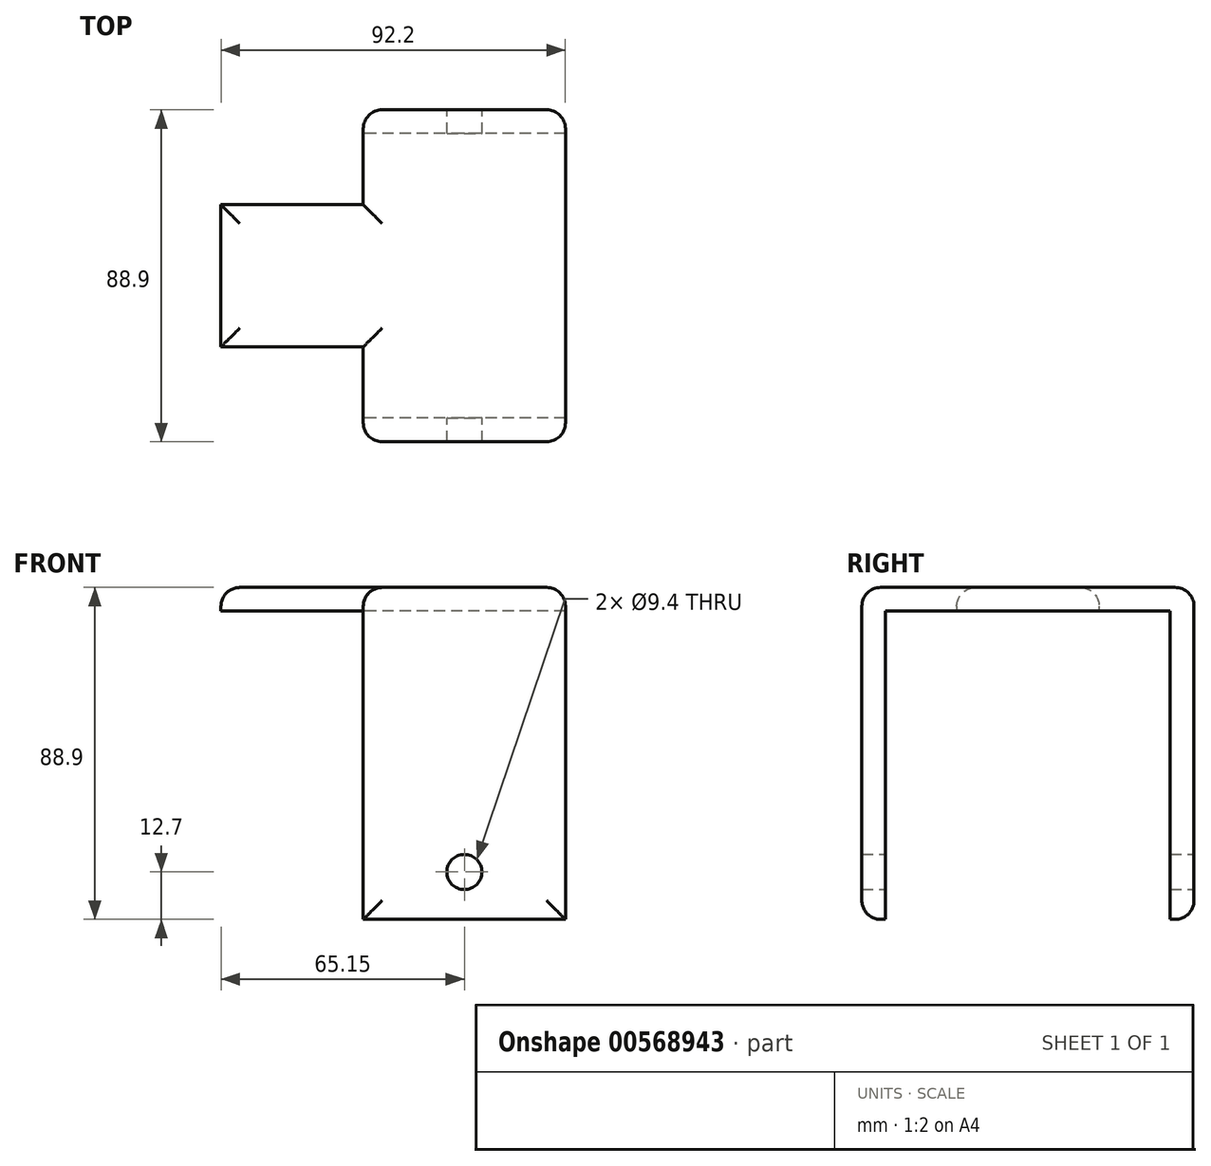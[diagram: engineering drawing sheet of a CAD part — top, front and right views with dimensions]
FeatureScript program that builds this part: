
annotation { "Feature Type Name" : "Feature", "Feature Type Description" : "" }
export const myFeature = defineFeature(function(context is Context, id is Id, definition is map)
    precondition{}
    {
        {
            var Q0;
            Q0=qCreatedBy(makeId("Front.planeOp"),FACE);
            var sketch = newSketch(context, id + "F0", { "sketchPlane" : qUnion([Q0])});
            skLineSegment(sketch, "E0.bottom", {"start": v(27.05, 44.45) * mm, "end": v(-27.05, 44.45) * mm});
            skLineSegment(sketch, "E0.top", {"start": v(27.05, -44.45) * mm, "end": v(-27.05, -44.45) * mm});
            skLineSegment(sketch, "E0.left", {"start": v(27.05, 44.45) * mm, "end": v(27.05, -44.45) * mm});
            skLineSegment(sketch, "E0.right", {"start": v(-27.05, 44.45) * mm, "end": v(-27.05, -44.45) * mm});
            skPoint(sketch, "E0.middle", {"position": v(0, 0) * mm});
            skSolve(sketch);
        }
        {
            var Q0;
            Q0=makeQuery(id+"F0.imprint","IMPRINT",FACE,{"disambiguationData":[TD([[makeQuery(id+"F0.imprint","IMPRINT",EDGE,{"derivedFrom":sQuery(id+"F0.wireOp",EDGE,"E0.bottom")}),1.0]])]});
            extrude(context, id + "F1", {"entities" : qUnion([Q0]), "depth" : 6.35 * mm, "offsetDistance" : 25.4 * mm});
        }
        {
            var Q0;
            Q0=makeQuery(id+"F1.opExtrude","CAP_FACE",FACE,{"disambiguationData":[OSD([sQuery(id+"F0.wireOp",EDGE,"E0.bottom"),sQuery(id+"F0.wireOp",EDGE,"E0.top"),sQuery(id+"F0.wireOp",EDGE,"E0.left"),sQuery(id+"F0.wireOp",EDGE,"E0.right")])],"isStart":true});
            var sketch = newSketch(context, id + "F2", { "sketchPlane" : qUnion([Q0])});
            skLineSegment(sketch, "E1.bottom", {"start": v(-27.05, 44.45) * mm, "end": v(27.05, 44.45) * mm});
            skLineSegment(sketch, "E1.top", {"start": v(-27.05, 38.1) * mm, "end": v(27.05, 38.1) * mm});
            skLineSegment(sketch, "E1.left", {"start": v(-27.05, 44.45) * mm, "end": v(-27.05, 38.1) * mm});
            skLineSegment(sketch, "E1.right", {"start": v(27.05, 44.45) * mm, "end": v(27.05, 38.1) * mm});
            skSolve(sketch);
        }
        {
            var Q0;
            Q0=makeQuery(id+"F2.imprint","IMPRINT",FACE,{"disambiguationData":[TD([[makeQuery(id+"F2.imprint","IMPRINT",EDGE,{"derivedFrom":sQuery(id+"F2.wireOp",EDGE,"E1.bottom")}),-1.0]])]});
            extrude(context, id + "F3", {"entities" : qUnion([Q0]), "operationType" : NewBodyOperationType.ADD, "depth" : 76.2 * mm, "offsetDistance" : 25.4 * mm});
        }
        {
            var Q0;
            Q0=makeQuery(id+"F3.opExtrude","CAP_FACE",FACE,{"disambiguationData":[OSD([sQuery(id+"F2.wireOp",EDGE,"E1.bottom"),sQuery(id+"F2.wireOp",EDGE,"E1.top"),sQuery(id+"F2.wireOp",EDGE,"E1.left"),sQuery(id+"F2.wireOp",EDGE,"E1.right")])],"isStart":false});
            var sketch = newSketch(context, id + "F4", { "sketchPlane" : qUnion([Q0])});
            skLineSegment(sketch, "E2.bottom", {"start": v(27.05, 44.45) * mm, "end": v(-27.05, 44.45) * mm});
            skLineSegment(sketch, "E2.top", {"start": v(27.05, -44.45) * mm, "end": v(-27.05, -44.45) * mm});
            skLineSegment(sketch, "E2.left", {"start": v(27.05, 44.45) * mm, "end": v(27.05, -44.45) * mm});
            skLineSegment(sketch, "E2.right", {"start": v(-27.05, 44.45) * mm, "end": v(-27.05, -44.45) * mm});
            skPoint(sketch, "E2.middle", {"position": v(0, 0) * mm});
            skSolve(sketch);
        }
        {
            var Q0;
            Q0 = qSketchRegion(id + "F4", true);
            extrude(context, id + "F5", {"entities" : qUnion([Q0]), "operationType" : NewBodyOperationType.ADD, "depth" : 6.35 * mm, "offsetDistance" : 25.4 * mm});
        }
        {
            var Q0;
            Q0=makeQuery(id+"F5.opExtrude","CAP_FACE",FACE,{"disambiguationData":[OSD([sQuery(id+"F4.wireOp",EDGE,"E2.bottom"),sQuery(id+"F4.wireOp",EDGE,"E2.top"),sQuery(id+"F4.wireOp",EDGE,"E2.left"),sQuery(id+"F4.wireOp",EDGE,"E2.right")])],"isStart":false});
            var sketch = newSketch(context, id + "F6", { "sketchPlane" : qUnion([Q0])});
            skLineSegment(sketch, "E3", {"start": v(0, -44.45) * mm, "end": v(0, -31.75) * mm, "construction": true});
            skCircle(sketch, "E4", {"center": v(0, -31.75) * mm, "radius": 4.7 * mm});
            skSolve(sketch);
        }
        {
            var Q0;
            Q0 = qSketchRegion(id + "F6", true);
            extrude(context, id + "F7", {"entities" : qUnion([Q0]), "operationType" : NewBodyOperationType.REMOVE, "oppositeDirection" : true, "depth" : 109.22 * mm, "offsetDistance" : 25.4 * mm});
        }
        {
            var Q0;
            Q0=makeQuery(id+"F5.boolean.opBoolean","MERGE",FACE,{"derivedFrom":[makeQuery(id+"F3.boolean.opBoolean","MERGE",FACE,{"derivedFrom":[makeQuery(id+"F1.opExtrude","SWEPT_FACE",FACE,{"disambiguationData":[OSD([sQuery(id+"F0.wireOp",EDGE,"E0.right")])]}),makeQuery(id+"F3.opExtrude","SWEPT_FACE",FACE,{"disambiguationData":[OSD([sQuery(id+"F2.wireOp",EDGE,"E1.right")])]})]}),makeQuery(id+"F5.opExtrude","SWEPT_FACE",FACE,{"disambiguationData":[OSD([sQuery(id+"F4.wireOp",EDGE,"E2.left")])]})]});
            var sketch = newSketch(context, id + "F8", { "sketchPlane" : qUnion([Q0])});
            skLineSegment(sketch, "E5", {"start": v(-38.1, 44.45) * mm, "end": v(-38.1, 38.1) * mm, "construction": true});
            skLineSegment(sketch, "E6.bottom", {"start": v(-19.05, 44.45) * mm, "end": v(-57.15, 44.45) * mm});
            skLineSegment(sketch, "E6.top", {"start": v(-19.05, 38.1) * mm, "end": v(-57.15, 38.1) * mm});
            skLineSegment(sketch, "E6.left", {"start": v(-19.05, 44.45) * mm, "end": v(-19.05, 38.1) * mm});
            skLineSegment(sketch, "E6.right", {"start": v(-57.15, 44.45) * mm, "end": v(-57.15, 38.1) * mm});
            skPoint(sketch, "E6.middle", {"position": v(-38.1, 41.28) * mm});
            skSolve(sketch);
        }
        {
            var Q0;
            Q0 = qSketchRegion(id + "F8", true);
            extrude(context, id + "F9", {"entities" : qUnion([Q0]), "operationType" : NewBodyOperationType.ADD, "depth" : 38.1 * mm, "offsetDistance" : 25.4 * mm});
        }
        {
            var Q0;
            Q0=makeQuery(id+"F5.opExtrude","CAP_EDGE",EDGE,{"disambiguationData":[OSD([sQuery(id+"F4.wireOp",EDGE,"E2.right")])],"isStart":false});
            var Q1;
            Q1=makeQuery(id+"F5.boolean.opBoolean","MERGE",EDGE,{"derivedFrom":[makeQuery(id+"F3.boolean.opBoolean","MERGE",EDGE,{"derivedFrom":[makeQuery(id+"F1.opExtrude","SWEPT_EDGE",EDGE,{"disambiguationData":[OSD([sQuery(id+"F0.wireOp",EDGE,"E0.bottom"),sQuery(id+"F0.wireOp",EDGE,"E0.left")])]}),makeQuery(id+"F3.opExtrude","SWEPT_EDGE",EDGE,{"disambiguationData":[OSD([sQuery(id+"F2.wireOp",EDGE,"E1.bottom"),sQuery(id+"F2.wireOp",EDGE,"E1.left")])]})]}),makeQuery(id+"F5.opExtrude","SWEPT_EDGE",EDGE,{"disambiguationData":[OSD([sQuery(id+"F4.wireOp",EDGE,"E2.bottom"),sQuery(id+"F4.wireOp",EDGE,"E2.right")])]})]});
            var Q2;
            Q2=makeQuery(id+"F5.opExtrude","CAP_EDGE",EDGE,{"disambiguationData":[OSD([sQuery(id+"F4.wireOp",EDGE,"E2.left")])],"isStart":false});
            var Q3;
            Q3=makeQuery(id+"F1.opExtrude","CAP_EDGE",EDGE,{"disambiguationData":[OSD([sQuery(id+"F0.wireOp",EDGE,"E0.right")])],"isStart":false});
            var Q4;
            Q4=makeQuery(id+"F1.opExtrude","CAP_EDGE",EDGE,{"disambiguationData":[OSD([sQuery(id+"F0.wireOp",EDGE,"E0.left")])],"isStart":false});
            var Q5;
            Q5=makeQuery(id+"F1.opExtrude","CAP_EDGE",EDGE,{"disambiguationData":[OSD([sQuery(id+"F0.wireOp",EDGE,"E0.top")])],"isStart":false});
            var Q6;
            Q6=makeQuery(id+"F5.opExtrude","CAP_EDGE",EDGE,{"disambiguationData":[OSD([sQuery(id+"F4.wireOp",EDGE,"E2.top")])],"isStart":false});
            var Q7;
            Q7=makeQuery(id+"F1.opExtrude","CAP_EDGE",EDGE,{"disambiguationData":[OSD([sQuery(id+"F0.wireOp",EDGE,"E0.bottom")])],"isStart":false});
            var Q8;
            Q8=makeQuery(id+"F5.opExtrude","CAP_EDGE",EDGE,{"disambiguationData":[OSD([sQuery(id+"F4.wireOp",EDGE,"E2.bottom")])],"isStart":false});
            var Q9;
            {var subQ0=sQuery(id+"F2.wireOp",EDGE,"E1.right");var subQ1=sQuery(id+"F4.wireOp",EDGE,"E2.bottom");var subQ2=sQuery(id+"F2.wireOp",EDGE,"E1.bottom");var subQ3=sQuery(id+"F0.wireOp",EDGE,"E0.right");var subQ4=sQuery(id+"F0.wireOp",EDGE,"E0.bottom");var subQ5=sQuery(id+"F4.wireOp",EDGE,"E2.left");Q9=makeQuery(id+"F9.boolean.opBoolean","SPLIT",EDGE,{"disambiguationData":[TD([makeQuery(id+"F9.opExtrude","SWEPT_FACE",FACE,{"disambiguationData":[OSD([sQuery(id+"F8.wireOp",EDGE,"E6.right")])]})])],"derivedFrom":makeQuery(id+"F5.boolean.opBoolean","MERGE",EDGE,{"derivedFrom":[makeQuery(id+"F3.boolean.opBoolean","MERGE",EDGE,{"derivedFrom":[makeQuery(id+"F1.opExtrude","SWEPT_EDGE",EDGE,{"disambiguationData":[OSD([subQ4,subQ3])]}),makeQuery(id+"F3.opExtrude","SWEPT_EDGE",EDGE,{"disambiguationData":[OSD([subQ2,subQ0])]})]}),makeQuery(id+"F5.opExtrude","SWEPT_EDGE",EDGE,{"disambiguationData":[OSD([subQ1,subQ5])]})]})});}
            var Q10;
            {var subQ0=sQuery(id+"F2.wireOp",EDGE,"E1.bottom");var subQ1=sQuery(id+"F0.wireOp",EDGE,"E0.right");var subQ2=sQuery(id+"F0.wireOp",EDGE,"E0.bottom");var subQ3=sQuery(id+"F2.wireOp",EDGE,"E1.right");var subQ4=sQuery(id+"F4.wireOp",EDGE,"E2.bottom");var subQ5=sQuery(id+"F4.wireOp",EDGE,"E2.left");Q10=makeQuery(id+"F9.boolean.opBoolean","SPLIT",EDGE,{"disambiguationData":[TD([makeQuery(id+"F9.opExtrude","SWEPT_FACE",FACE,{"disambiguationData":[OSD([sQuery(id+"F8.wireOp",EDGE,"E6.left")])]})])],"derivedFrom":makeQuery(id+"F5.boolean.opBoolean","MERGE",EDGE,{"derivedFrom":[makeQuery(id+"F3.boolean.opBoolean","MERGE",EDGE,{"derivedFrom":[makeQuery(id+"F1.opExtrude","SWEPT_EDGE",EDGE,{"disambiguationData":[OSD([subQ2,subQ1])]}),makeQuery(id+"F3.opExtrude","SWEPT_EDGE",EDGE,{"disambiguationData":[OSD([subQ0,subQ3])]})]}),makeQuery(id+"F5.opExtrude","SWEPT_EDGE",EDGE,{"disambiguationData":[OSD([subQ4,subQ5])]})]})});}
            var Q11;
            Q11=makeQuery(id+"F9.opExtrude","CAP_EDGE",EDGE,{"disambiguationData":[OSD([sQuery(id+"F8.wireOp",EDGE,"E6.bottom")])],"isStart":false});
            var Q12;
            Q12=makeQuery(id+"F9.opExtrude","SWEPT_EDGE",EDGE,{"disambiguationData":[OSD([sQuery(id+"F0.wireOp",EDGE,"E0.bottom"),sQuery(id+"F0.wireOp",EDGE,"E0.right"),sQuery(id+"F2.wireOp",EDGE,"E1.bottom"),sQuery(id+"F2.wireOp",EDGE,"E1.right"),sQuery(id+"F4.wireOp",EDGE,"E2.bottom"),sQuery(id+"F4.wireOp",EDGE,"E2.left"),sQuery(id+"F8.wireOp",EDGE,"E6.bottom"),sQuery(id+"F8.wireOp",EDGE,"E6.left")])]});
            var Q13;
            Q13=makeQuery(id+"F9.opExtrude","SWEPT_EDGE",EDGE,{"disambiguationData":[OSD([sQuery(id+"F0.wireOp",EDGE,"E0.bottom"),sQuery(id+"F0.wireOp",EDGE,"E0.right"),sQuery(id+"F2.wireOp",EDGE,"E1.bottom"),sQuery(id+"F2.wireOp",EDGE,"E1.right"),sQuery(id+"F4.wireOp",EDGE,"E2.bottom"),sQuery(id+"F4.wireOp",EDGE,"E2.left"),sQuery(id+"F8.wireOp",EDGE,"E6.bottom"),sQuery(id+"F8.wireOp",EDGE,"E6.right")])]});
            fillet(context, id + "F10", {"entities" : qUnion([Q0, Q1, Q2, Q3, Q4, Q5, Q6, Q7, Q8, Q9, Q10, Q11, Q12, Q13]), "radius" : 5.08 * mm, "tangentPropagation" : true, "allowEdgeOverflow" : false});
        }
    });
